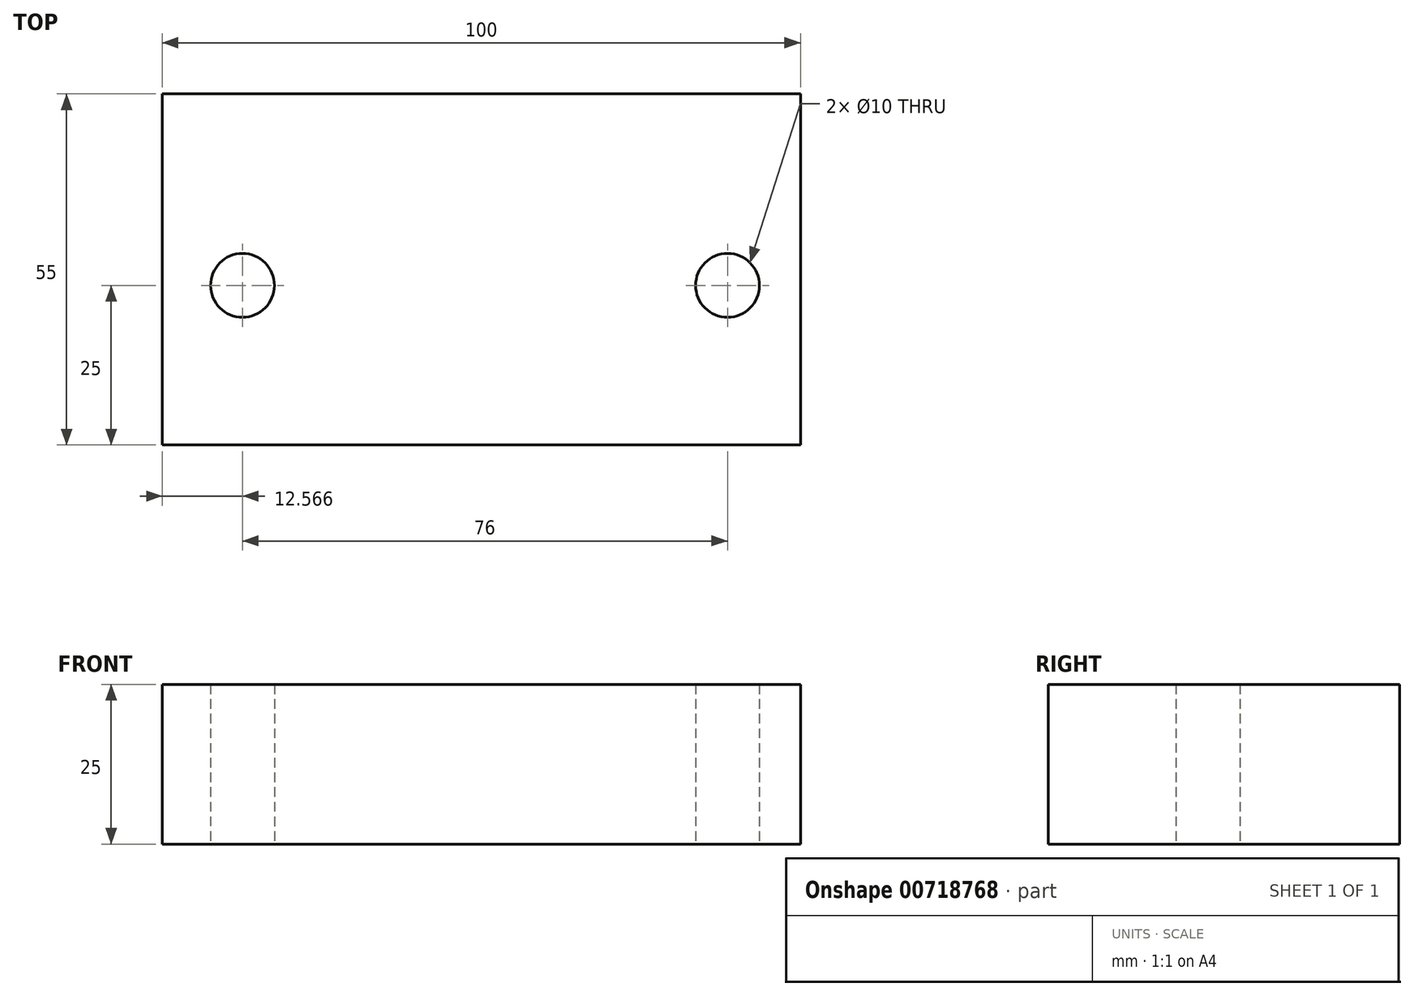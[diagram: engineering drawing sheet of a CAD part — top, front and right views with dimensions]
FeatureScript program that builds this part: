
annotation { "Feature Type Name" : "Feature", "Feature Type Description" : "" }
export const myFeature = defineFeature(function(context is Context, id is Id, definition is map)
    precondition{}
    {
        {
            var Q0;
            Q0=qCreatedBy(makeId("Top.planeOp"),FACE);
            var sketch = newSketch(context, id + "F0", { "sketchPlane" : qUnion([Q0])});
            skLineSegment(sketch, "E0.bottom", {"start": v(0, 55) * mm, "end": v(-100, 55) * mm});
            skLineSegment(sketch, "E0.top", {"start": v(0, 0) * mm, "end": v(-100, 0) * mm});
            skLineSegment(sketch, "E0.left", {"start": v(0, 55) * mm, "end": v(0, 0) * mm});
            skLineSegment(sketch, "E0.right", {"start": v(-100, 55) * mm, "end": v(-100, 0) * mm});
            skSolve(sketch);
        }
        {
            var Q0;
            Q0=makeQuery(id+"F0.imprint","IMPRINT",FACE,{"disambiguationData":[TD([[makeQuery(id+"F0.imprint","IMPRINT",EDGE,{"derivedFrom":sQuery(id+"F0.wireOp",EDGE,"E0.bottom")}),1.0]])]});
            extrude(context, id + "F1", {"entities" : qUnion([Q0]), "depth" : 25 * mm, "offsetDistance" : 25 * mm});
        }
        {
            var Q0;
            Q0=qCreatedBy(makeId("Top.planeOp"),FACE);
            var sketch = newSketch(context, id + "F2", { "sketchPlane" : qUnion([Q0])});
            skCircle(sketch, "E1", {"center": v(-87.43, 25) * mm, "radius": 5 * mm});
            skCircle(sketch, "E2.1.0.0", {"center": v(-49.43, 25) * mm, "radius": 5 * mm});
            skCircle(sketch, "E2.2.0.0", {"center": v(-11.43, 25) * mm, "radius": 5 * mm});
            skLineSegment(sketch, "E2.direction1", {"start": v(-87.43, 25) * mm, "end": v(-49.43, 25) * mm, "construction": true});
            skSolve(sketch);
        }
        {
            var Q0;
            Q0=makeQuery(id+"F2.imprint","IMPRINT",FACE,{"disambiguationData":[TD([[makeQuery(id+"F2.imprint","IMPRINT",EDGE,{"derivedFrom":sQuery(id+"F2.wireOp",EDGE,"E1")}),1.0]])]});
            var Q1;
            Q1=makeQuery(id+"F2.imprint","IMPRINT",FACE,{"disambiguationData":[TD([[makeQuery(id+"F2.imprint","IMPRINT",EDGE,{"derivedFrom":sQuery(id+"F2.wireOp",EDGE,"E2.2.0.0")}),1.0]])]});
            var Q2;
            Q2=sQuery(id+"F2.wireOp",EDGE,"E1");
            var Q3;
            Q3=sQuery(id+"F2.wireOp",EDGE,"E2.1.0.0");
            var Q4;
            Q4=sQuery(id+"F2.wireOp",EDGE,"E2.2.0.0");
            extrude(context, id + "F3", {"entities" : qUnion([Q0, Q1]), "operationType" : NewBodyOperationType.REMOVE, "surfaceEntities" : qUnion([Q2, Q3, Q4]), "depth" : 25 * mm, "offsetDistance" : 25 * mm});
        }
    });
